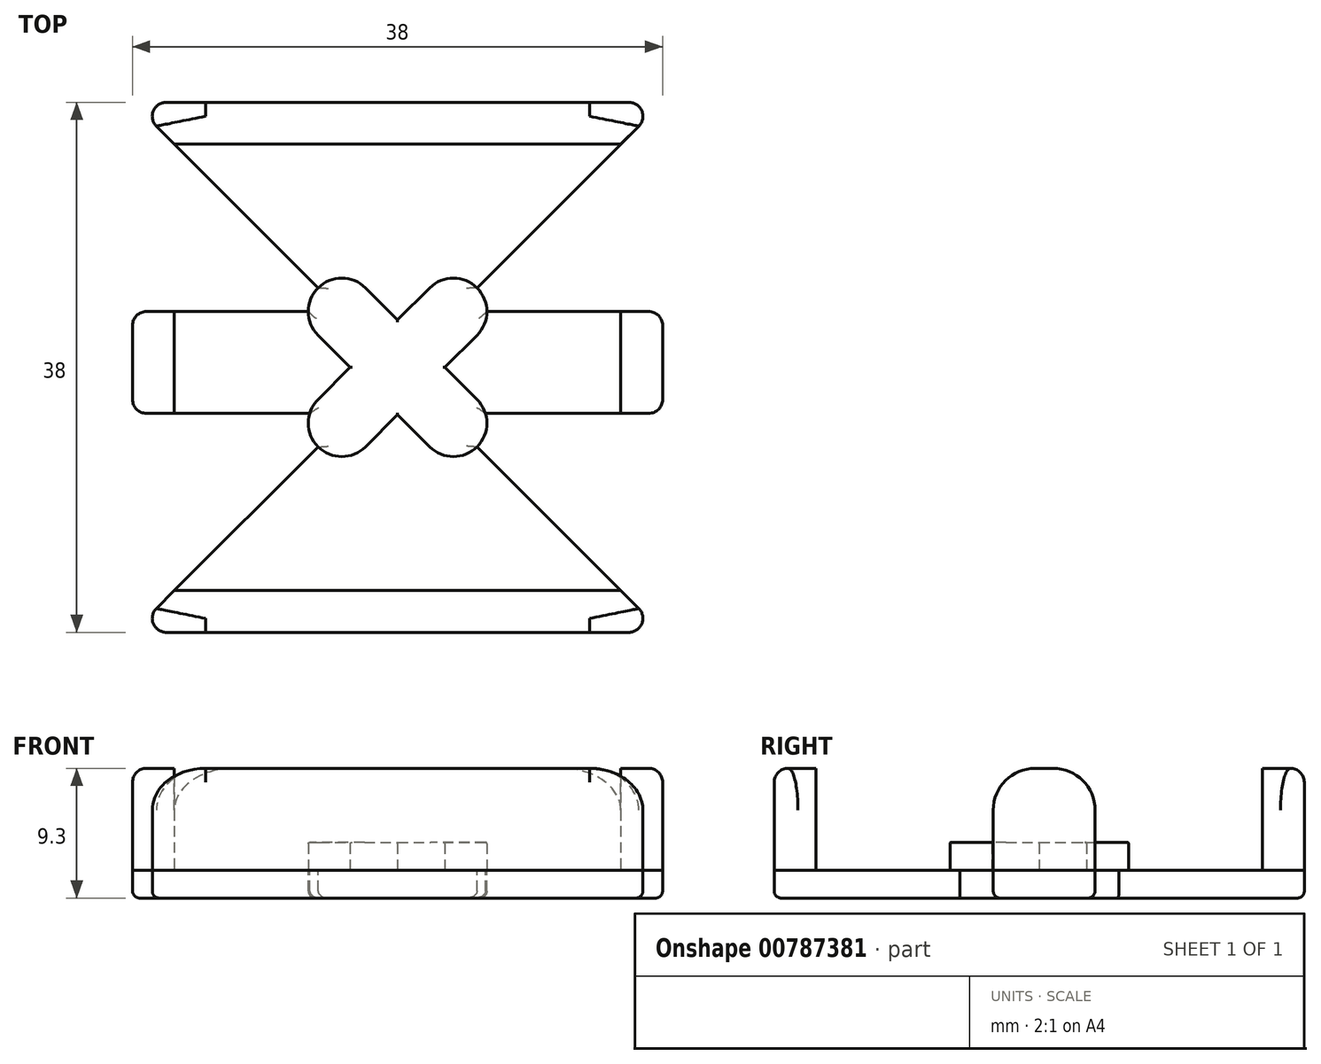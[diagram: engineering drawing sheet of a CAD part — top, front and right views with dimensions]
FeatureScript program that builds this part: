
annotation { "Feature Type Name" : "Feature", "Feature Type Description" : "" }
export const myFeature = defineFeature(function(context is Context, id is Id, definition is map)
    precondition{}
    {
        {
            var Q0;
            Q0=qCreatedBy(makeId("Top.planeOp"),FACE);
            var sketch = newSketch(context, id + "F0", { "sketchPlane" : qUnion([Q0])});
            skArc(sketch, "E0", {"start": v(1.7, 1.7) * mm, "mid": v(-1.7, 1.7) * mm, "end": v(-1.7, -1.7) * mm});
            skArc(sketch, "E1", {"start": v(9.7, -1.7) * mm, "mid": v(9.7, 1.7) * mm, "end": v(6.3, 1.7) * mm});
            skArc(sketch, "E2", {"start": v(6.3, -9.7) * mm, "mid": v(9.7, -9.7) * mm, "end": v(9.7, -6.3) * mm});
            skArc(sketch, "E3", {"start": v(-1.7, -6.3) * mm, "mid": v(-1.7, -9.7) * mm, "end": v(1.7, -9.7) * mm});
            skLineSegment(sketch, "E4", {"start": v(-1.7, -6.3) * mm, "end": v(0.6, -4) * mm});
            skLineSegment(sketch, "E5", {"start": v(1.7, -9.7) * mm, "end": v(4, -7.4) * mm});
            skLineSegment(sketch, "E6", {"start": v(1.7, 1.7) * mm, "end": v(4, -0.6) * mm});
            skLineSegment(sketch, "E7", {"start": v(-1.7, -1.7) * mm, "end": v(0.6, -4) * mm});
            skLineSegment(sketch, "E8.trimOffspring", {"start": v(4, -0.6) * mm, "end": v(6.3, 1.7) * mm});
            skLineSegment(sketch, "E9.trimOffspring", {"start": v(4, -7.4) * mm, "end": v(6.3, -9.7) * mm});
            skLineSegment(sketch, "E10.trimOffspring", {"start": v(7.4, -4) * mm, "end": v(9.7, -6.3) * mm});
            skLineSegment(sketch, "E11.trimOffspring", {"start": v(7.4, -4) * mm, "end": v(9.7, -1.7) * mm});
            skSolve(sketch);
        }
        {
            var Q0;
            Q0=makeQuery(id+"F0.imprint","IMPRINT",FACE,{"disambiguationData":[TD([[makeQuery(id+"F0.imprint","IMPRINT",EDGE,{"derivedFrom":sQuery(id+"F0.wireOp",EDGE,"E0")}),1.0]])]});
            extrude(context, id + "F1", {"entities" : qUnion([Q0]), "depth" : 2 * mm, "offsetDistance" : 25 * mm});
        }
        {
            var Q0;
            Q0=qCreatedBy(makeId("Top.planeOp"),FACE);
            var sketch = newSketch(context, id + "F2", { "sketchPlane" : qUnion([Q0])});
            skLineSegment(sketch, "E12.bottom", {"start": v(-9, 12) * mm, "end": v(17, 12) * mm});
            skLineSegment(sketch, "E12.top", {"start": v(-9, -20) * mm, "end": v(17, -20) * mm});
            skLineSegment(sketch, "E12.left", {"start": v(-12, 9) * mm, "end": v(-12, -17) * mm});
            skLineSegment(sketch, "E12.right", {"start": v(20, 9) * mm, "end": v(20, -17) * mm});
            skLineSegment(sketch, "E13", {"start": v(4, -0.6) * mm, "end": v(4, -7.4) * mm});
            skLineSegment(sketch, "E14", {"start": v(0.6, -4) * mm, "end": v(7.4, -4) * mm});
            skPoint(sketch, "E15", {"position": v(4, -4) * mm});
            skPoint(sketch, "E16", {"position": v(4, 12) * mm});
            skPoint(sketch, "E17", {"position": v(-12, -4) * mm});
            skPoint(sketch, "E18.visualSharp", {"position": v(-12, 12) * mm});
            skArc(sketch, "E18.filletArc", {"start": v(-9, 12) * mm, "mid": v(-11.12, 11.12) * mm, "end": v(-12, 9) * mm});
            skPoint(sketch, "E19.visualSharp", {"position": v(20, 12) * mm});
            skArc(sketch, "E19.filletArc", {"start": v(20, 9) * mm, "mid": v(19.12, 11.12) * mm, "end": v(17, 12) * mm});
            skPoint(sketch, "E20.visualSharp", {"position": v(20, -20) * mm});
            skArc(sketch, "E20.filletArc", {"start": v(17, -20) * mm, "mid": v(19.12, -19.12) * mm, "end": v(20, -17) * mm});
            skPoint(sketch, "E21.visualSharp", {"position": v(-12, -20) * mm});
            skArc(sketch, "E21.filletArc", {"start": v(-12, -17) * mm, "mid": v(-11.12, -19.12) * mm, "end": v(-9, -20) * mm});
            skSolve(sketch);
        }
        {
            var Q0;
            Q0=qCreatedBy(makeId("Top.planeOp"),FACE);
            var sketch = newSketch(context, id + "F3", { "sketchPlane" : qUnion([Q0])});
            skLineSegment(sketch, "E22", {"start": v(4, -4) * mm, "end": v(-15, -23) * mm});
            skLineSegment(sketch, "E23", {"start": v(4, -4) * mm, "end": v(23, -23) * mm});
            skLineSegment(sketch, "E24", {"start": v(-15, -23) * mm, "end": v(23, -23) * mm});
            skLineSegment(sketch, "E25", {"start": v(4, -4) * mm, "end": v(-15, 15) * mm});
            skLineSegment(sketch, "E26", {"start": v(4, -4) * mm, "end": v(23, 15) * mm});
            skLineSegment(sketch, "E27", {"start": v(10.4, 0) * mm, "end": v(23, 0) * mm});
            skLineSegment(sketch, "E28", {"start": v(10.3, -7.3) * mm, "end": v(23, -7.3) * mm});
            skLineSegment(sketch, "E29", {"start": v(23, 0) * mm, "end": v(23, -7.3) * mm});
            skLineSegment(sketch, "E30", {"start": v(-2.4, 0) * mm, "end": v(-15, 0) * mm});
            skLineSegment(sketch, "E31", {"start": v(-2.3, -7.3) * mm, "end": v(-15, -7.3) * mm});
            skLineSegment(sketch, "E32", {"start": v(-15, 0) * mm, "end": v(-15, -7.3) * mm});
            skLineSegment(sketch, "E33", {"start": v(-15, 15) * mm, "end": v(23, 15) * mm});
            skLineSegment(sketch, "E34", {"start": v(4, -4) * mm, "end": v(0.7, -7.3) * mm});
            skLineSegment(sketch, "E35", {"start": v(8, 0) * mm, "end": v(4, -4) * mm});
            skLineSegment(sketch, "E36", {"start": v(4, -4) * mm, "end": v(7.26, -7.26) * mm});
            skLineSegment(sketch, "E37", {"start": v(4, -4) * mm, "end": v(0, 0) * mm});
            skArc(sketch, "E38", {"start": v(-1.7, 1.7) * mm, "mid": v(-2.22, 0.92) * mm, "end": v(-2.4, 0) * mm});
            skArc(sketch, "E39", {"start": v(-2.3, -7.3) * mm, "mid": v(-2.33, -8.58) * mm, "end": v(-1.7, -9.7) * mm});
            skArc(sketch, "E40", {"start": v(10.4, 0) * mm, "mid": v(10.22, 0.92) * mm, "end": v(9.7, 1.7) * mm});
            skArc(sketch, "E41", {"start": v(9.7, -9.7) * mm, "mid": v(10.33, -8.58) * mm, "end": v(10.3, -7.3) * mm});
            skSolve(sketch);
        }
        {
            var Q0;
            Q0=makeQuery(id+"F3.imprint","IMPRINT",FACE,{"disambiguationData":[TD([[makeQuery(id+"F3.imprint","IMPRINT",EDGE,{"derivedFrom":sQuery(id+"F3.wireOp",EDGE,"E25")}),-1.0]])]});
            var Q1;
            Q1=makeQuery(id+"F3.imprint","IMPRINT",FACE,{"disambiguationData":[TD([[makeQuery(id+"F3.imprint","IMPRINT",EDGE,{"derivedFrom":sQuery(id+"F3.wireOp",EDGE,"E27")}),-1.0]])]});
            var Q2;
            Q2=makeQuery(id+"F3.imprint","IMPRINT",FACE,{"disambiguationData":[TD([[makeQuery(id+"F3.imprint","IMPRINT",EDGE,{"derivedFrom":sQuery(id+"F3.wireOp",EDGE,"E30")}),1.0]])]});
            var Q3;
            Q3=makeQuery(id+"F3.imprint","IMPRINT",FACE,{"disambiguationData":[TD([[makeQuery(id+"F3.imprint","IMPRINT",EDGE,{"derivedFrom":sQuery(id+"F3.wireOp",EDGE,"E22")}),1.0]])]});
            extrude(context, id + "F4", {"entities" : qUnion([Q0, Q1, Q2, Q3]), "oppositeDirection" : true, "depth" : 2 * mm, "offsetDistance" : 25 * mm});
        }
        {
            var Q0;
            Q0=qCreatedBy(makeId("Top.planeOp"),FACE);
            var sketch = newSketch(context, id + "F5", { "sketchPlane" : qUnion([Q0])});
            skLineSegment(sketch, "E42", {"start": v(-15, 15) * mm, "end": v(23, 15) * mm});
            skLineSegment(sketch, "E43", {"start": v(23, 15) * mm, "end": v(20, 12) * mm});
            skLineSegment(sketch, "E44", {"start": v(-15, 15) * mm, "end": v(-12, 12) * mm});
            skLineSegment(sketch, "E45", {"start": v(20, 12) * mm, "end": v(-12, 12) * mm});
            skLineSegment(sketch, "E46.bottom", {"start": v(23, 0) * mm, "end": v(20, 0) * mm});
            skLineSegment(sketch, "E46.top", {"start": v(23, -7.3) * mm, "end": v(20, -7.3) * mm});
            skLineSegment(sketch, "E46.left", {"start": v(23, 0) * mm, "end": v(23, -7.3) * mm});
            skLineSegment(sketch, "E46.right", {"start": v(20, 0) * mm, "end": v(20, -7.3) * mm});
            skLineSegment(sketch, "E47.bottom", {"start": v(-15, 0) * mm, "end": v(-12, 0) * mm});
            skLineSegment(sketch, "E47.top", {"start": v(-15, -7.3) * mm, "end": v(-12, -7.3) * mm});
            skLineSegment(sketch, "E47.left", {"start": v(-15, 0) * mm, "end": v(-15, -7.3) * mm});
            skLineSegment(sketch, "E47.right", {"start": v(-12, 0) * mm, "end": v(-12, -7.3) * mm});
            skLineSegment(sketch, "E48", {"start": v(-15, -23) * mm, "end": v(23, -23) * mm});
            skLineSegment(sketch, "E49", {"start": v(23, -23) * mm, "end": v(20, -20) * mm});
            skLineSegment(sketch, "E50", {"start": v(-15, -23) * mm, "end": v(-12, -20) * mm});
            skLineSegment(sketch, "E51", {"start": v(20, -20) * mm, "end": v(-12, -20) * mm});
            skSolve(sketch);
        }
        {
            var Q0;
            Q0=makeQuery(id+"F5.imprint","IMPRINT",FACE,{"disambiguationData":[TD([[makeQuery(id+"F5.imprint","IMPRINT",EDGE,{"derivedFrom":sQuery(id+"F5.wireOp",EDGE,"E42")}),-1.0]])]});
            var Q1;
            Q1=makeQuery(id+"F5.imprint","IMPRINT",FACE,{"disambiguationData":[TD([[makeQuery(id+"F5.imprint","IMPRINT",EDGE,{"derivedFrom":sQuery(id+"F5.wireOp",EDGE,"E47.bottom")}),-1.0]])]});
            var Q2;
            Q2=makeQuery(id+"F5.imprint","IMPRINT",FACE,{"disambiguationData":[TD([[makeQuery(id+"F5.imprint","IMPRINT",EDGE,{"derivedFrom":sQuery(id+"F5.wireOp",EDGE,"E46.bottom")}),1.0]])]});
            var Q3;
            Q3=makeQuery(id+"F5.imprint","IMPRINT",FACE,{"disambiguationData":[TD([[makeQuery(id+"F5.imprint","IMPRINT",EDGE,{"derivedFrom":sQuery(id+"F5.wireOp",EDGE,"E48")}),1.0]])]});
            extrude(context, id + "F6", {"entities" : qUnion([Q0, Q1, Q2, Q3]), "depth" : 7.3 * mm, "offsetDistance" : 25 * mm});
        }
        {
            var Q0;
            Q0=makeQuery(id+"F6.opExtrude","CAP_EDGE",EDGE,{"disambiguationData":[OSD([sQuery(id+"F5.wireOp",EDGE,"E46.bottom")])],"isStart":false});
            var Q1;
            Q1=makeQuery(id+"F6.opExtrude","CAP_EDGE",EDGE,{"disambiguationData":[OSD([sQuery(id+"F5.wireOp",EDGE,"E46.top")])],"isStart":false});
            var Q2;
            Q2=makeQuery(id+"F6.opExtrude","CAP_EDGE",EDGE,{"disambiguationData":[OSD([sQuery(id+"F5.wireOp",EDGE,"E47.bottom")])],"isStart":false});
            var Q3;
            Q3=makeQuery(id+"F6.opExtrude","CAP_EDGE",EDGE,{"disambiguationData":[OSD([sQuery(id+"F5.wireOp",EDGE,"E47.top")])],"isStart":false});
            var Q4;
            Q4=makeQuery(id+"F6.opExtrude","CAP_EDGE",EDGE,{"disambiguationData":[OSD([sQuery(id+"F5.wireOp",EDGE,"E50")])],"isStart":false});
            var Q5;
            Q5=makeQuery(id+"F6.opExtrude","CAP_EDGE",EDGE,{"disambiguationData":[OSD([sQuery(id+"F5.wireOp",EDGE,"E49")])],"isStart":false});
            var Q6;
            Q6=makeQuery(id+"F6.opExtrude","CAP_EDGE",EDGE,{"disambiguationData":[OSD([sQuery(id+"F5.wireOp",EDGE,"E44")])],"isStart":false});
            var Q7;
            Q7=makeQuery(id+"F6.opExtrude","CAP_EDGE",EDGE,{"disambiguationData":[OSD([sQuery(id+"F5.wireOp",EDGE,"E43")])],"isStart":false});
            fillet(context, id + "F7", {"entities" : qUnion([Q0, Q1, Q2, Q3, Q4, Q5, Q6, Q7]), "radius" : 3 * mm, "tangentPropagation" : true, "allowEdgeOverflow" : false});
        }
        {
            var Q0;
            Q0=makeQuery(id+"F4.opExtrude","SWEPT_EDGE",EDGE,{"disambiguationData":[OSD([sQuery(id+"F3.wireOp",EDGE,"E30"),sQuery(id+"F3.wireOp",EDGE,"E32")])]});
            var Q1;
            Q1=makeQuery(id+"F6.opExtrude","SWEPT_EDGE",EDGE,{"disambiguationData":[OSD([sQuery(id+"F5.wireOp",EDGE,"E47.bottom"),sQuery(id+"F5.wireOp",EDGE,"E47.left")])]});
            var Q2;
            Q2=makeQuery(id+"F4.opExtrude","SWEPT_EDGE",EDGE,{"disambiguationData":[OSD([sQuery(id+"F3.wireOp",EDGE,"E31"),sQuery(id+"F3.wireOp",EDGE,"E32")])]});
            var Q3;
            Q3=makeQuery(id+"F4.opExtrude","SWEPT_EDGE",EDGE,{"disambiguationData":[OSD([sQuery(id+"F3.wireOp",EDGE,"E28"),sQuery(id+"F3.wireOp",EDGE,"E29")])]});
            var Q4;
            Q4=makeQuery(id+"F6.opExtrude","SWEPT_EDGE",EDGE,{"disambiguationData":[OSD([sQuery(id+"F5.wireOp",EDGE,"E46.top"),sQuery(id+"F5.wireOp",EDGE,"E46.left")])]});
            var Q5;
            Q5=makeQuery(id+"F4.opExtrude","SWEPT_EDGE",EDGE,{"disambiguationData":[OSD([sQuery(id+"F3.wireOp",EDGE,"E27"),sQuery(id+"F3.wireOp",EDGE,"E29")])]});
            var Q6;
            Q6=makeQuery(id+"F6.opExtrude","SWEPT_EDGE",EDGE,{"disambiguationData":[OSD([sQuery(id+"F5.wireOp",EDGE,"E42"),sQuery(id+"F5.wireOp",EDGE,"E43")])]});
            var Q7;
            Q7=makeQuery(id+"F4.opExtrude","SWEPT_EDGE",EDGE,{"disambiguationData":[OSD([sQuery(id+"F3.wireOp",EDGE,"E26"),sQuery(id+"F3.wireOp",EDGE,"E33")])]});
            var Q8;
            Q8=makeQuery(id+"F4.opExtrude","SWEPT_EDGE",EDGE,{"disambiguationData":[OSD([sQuery(id+"F3.wireOp",EDGE,"E25"),sQuery(id+"F3.wireOp",EDGE,"E33")])]});
            var Q9;
            Q9=makeQuery(id+"F4.opExtrude","SWEPT_EDGE",EDGE,{"disambiguationData":[OSD([sQuery(id+"F3.wireOp",EDGE,"E23"),sQuery(id+"F3.wireOp",EDGE,"E24")])]});
            var Q10;
            Q10=makeQuery(id+"F6.opExtrude","SWEPT_EDGE",EDGE,{"disambiguationData":[OSD([sQuery(id+"F5.wireOp",EDGE,"E48"),sQuery(id+"F5.wireOp",EDGE,"E49")])]});
            var Q11;
            Q11=makeQuery(id+"F4.opExtrude","SWEPT_EDGE",EDGE,{"disambiguationData":[OSD([sQuery(id+"F3.wireOp",EDGE,"E22"),sQuery(id+"F3.wireOp",EDGE,"E24")])]});
            fillet(context, id + "F8", {"entities" : qUnion([Q0, Q1, Q2, Q3, Q4, Q5, Q6, Q7, Q8, Q9, Q10, Q11]), "radius" : 1 * mm, "tangentPropagation" : true, "allowEdgeOverflow" : false});
        }
        {
            var Q0;
            {var subQ0=sQuery(id+"F3.wireOp",EDGE,"E33");var subQ1=sQuery(id+"F3.wireOp",EDGE,"E25");Q0=makeQuery(id+"F8.opFillet","BLEND_EDGE",EDGE,{"blendedFrom":[makeQuery(id+"F4.opExtrude","SWEPT_EDGE",EDGE,{"disambiguationData":[OSD([subQ1,subQ0])]}),makeQuery(id+"F4.opExtrude","CAP_FACE",FACE,{"disambiguationData":[OSD([sQuery(id+"F3.wireOp",EDGE,"E22"),sQuery(id+"F3.wireOp",EDGE,"E23"),sQuery(id+"F3.wireOp",EDGE,"E24"),subQ1,sQuery(id+"F3.wireOp",EDGE,"E26"),sQuery(id+"F3.wireOp",EDGE,"E27"),sQuery(id+"F3.wireOp",EDGE,"E28"),sQuery(id+"F3.wireOp",EDGE,"E29"),sQuery(id+"F3.wireOp",EDGE,"E30"),sQuery(id+"F3.wireOp",EDGE,"E31"),sQuery(id+"F3.wireOp",EDGE,"E32"),subQ0,sQuery(id+"F3.wireOp",EDGE,"E38"),sQuery(id+"F3.wireOp",EDGE,"E39"),sQuery(id+"F3.wireOp",EDGE,"E40"),sQuery(id+"F3.wireOp",EDGE,"E41")])],"isStart":false})],"blendedInto":[makeQuery(id+"F4.opExtrude","CAP_FACE",FACE,{"disambiguationData":[OSD([sQuery(id+"F3.wireOp",EDGE,"E22"),sQuery(id+"F3.wireOp",EDGE,"E23"),sQuery(id+"F3.wireOp",EDGE,"E24"),subQ1,sQuery(id+"F3.wireOp",EDGE,"E26"),sQuery(id+"F3.wireOp",EDGE,"E27"),sQuery(id+"F3.wireOp",EDGE,"E28"),sQuery(id+"F3.wireOp",EDGE,"E29"),sQuery(id+"F3.wireOp",EDGE,"E30"),sQuery(id+"F3.wireOp",EDGE,"E31"),sQuery(id+"F3.wireOp",EDGE,"E32"),subQ0,sQuery(id+"F3.wireOp",EDGE,"E38"),sQuery(id+"F3.wireOp",EDGE,"E39"),sQuery(id+"F3.wireOp",EDGE,"E40"),sQuery(id+"F3.wireOp",EDGE,"E41")])],"isStart":false})]});}
            var Q1;
            Q1=makeQuery(id+"F4.opExtrude","CAP_EDGE",EDGE,{"disambiguationData":[OSD([sQuery(id+"F3.wireOp",EDGE,"E38")])],"isStart":false});
            var Q2;
            Q2=makeQuery(id+"F4.opExtrude","CAP_EDGE",EDGE,{"disambiguationData":[OSD([sQuery(id+"F3.wireOp",EDGE,"E30")])],"isStart":false});
            var Q3;
            Q3=makeQuery(id+"F4.opExtrude","CAP_EDGE",EDGE,{"disambiguationData":[OSD([sQuery(id+"F3.wireOp",EDGE,"E39")])],"isStart":false});
            var Q4;
            Q4=makeQuery(id+"F4.opExtrude","CAP_EDGE",EDGE,{"disambiguationData":[OSD([sQuery(id+"F3.wireOp",EDGE,"E22")])],"isStart":false});
            var Q5;
            Q5=makeQuery(id+"F4.opExtrude","CAP_EDGE",EDGE,{"disambiguationData":[OSD([sQuery(id+"F3.wireOp",EDGE,"E41")])],"isStart":false});
            var Q6;
            Q6=makeQuery(id+"F4.opExtrude","CAP_EDGE",EDGE,{"disambiguationData":[OSD([sQuery(id+"F3.wireOp",EDGE,"E28")])],"isStart":false});
            var Q7;
            Q7=makeQuery(id+"F4.opExtrude","CAP_EDGE",EDGE,{"disambiguationData":[OSD([sQuery(id+"F3.wireOp",EDGE,"E40")])],"isStart":false});
            fillet(context, id + "F9", {"entities" : qUnion([Q0, Q1, Q2, Q3, Q4, Q5, Q6, Q7]), "radius" : 0.5 * mm, "tangentPropagation" : true, "allowEdgeOverflow" : false});
        }
        {
            var Q0;
            Q0=makeQuery(id+"F1.opExtrude","CAP_EDGE",EDGE,{"disambiguationData":[OSD([sQuery(id+"F0.wireOp",EDGE,"E10.trimOffspring")])],"isStart":false});
            var Q1;
            Q1=makeQuery(id+"F1.opExtrude","CAP_EDGE",EDGE,{"disambiguationData":[OSD([sQuery(id+"F0.wireOp",EDGE,"E2")])],"isStart":false});
            var Q2;
            Q2=makeQuery(id+"F1.opExtrude","CAP_EDGE",EDGE,{"disambiguationData":[OSD([sQuery(id+"F0.wireOp",EDGE,"E9.trimOffspring")])],"isStart":false});
            var Q3;
            Q3=makeQuery(id+"F1.opExtrude","CAP_EDGE",EDGE,{"disambiguationData":[OSD([sQuery(id+"F0.wireOp",EDGE,"E5")])],"isStart":false});
            var Q4;
            Q4=makeQuery(id+"F1.opExtrude","CAP_EDGE",EDGE,{"disambiguationData":[OSD([sQuery(id+"F0.wireOp",EDGE,"E7")])],"isStart":false});
            var Q5;
            Q5=makeQuery(id+"F1.opExtrude","CAP_EDGE",EDGE,{"disambiguationData":[OSD([sQuery(id+"F0.wireOp",EDGE,"E1")])],"isStart":false});
            fillet(context, id + "F10", {"entities" : qUnion([Q0, Q1, Q2, Q3, Q4, Q5]), "radius" : 0.1 * mm, "tangentPropagation" : true, "allowEdgeOverflow" : false});
        }
    });
